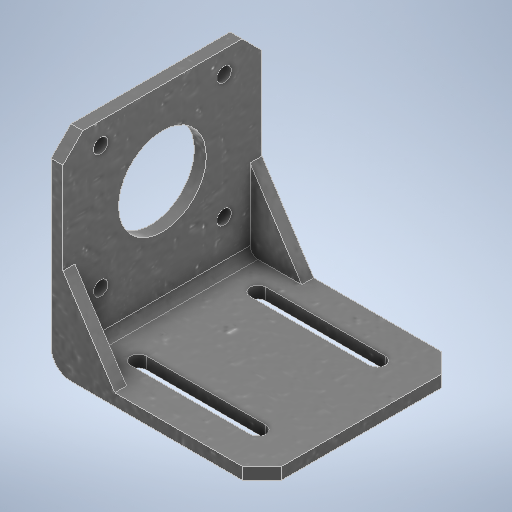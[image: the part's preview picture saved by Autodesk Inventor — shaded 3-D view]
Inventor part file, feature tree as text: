
AUTODESK INVENTOR PART (.ipt)
format: ipt  version: 2025.2 (Build 292293000, 293)  size: 432,128 bytes
history: native  units: in
note: dims shown in document units (in); Inventor stores cm internally (conversion verified against a paired STEP export)
features: mirror x1
ambient origin geometry x8: Origin, YZ Plane, XZ Plane, XY Plane, X Axis, Y Axis, Z Axis, Center Point
bodies: Solid1 (feature_tree)
feature tree (1):
  mirror  "Mirror1"
